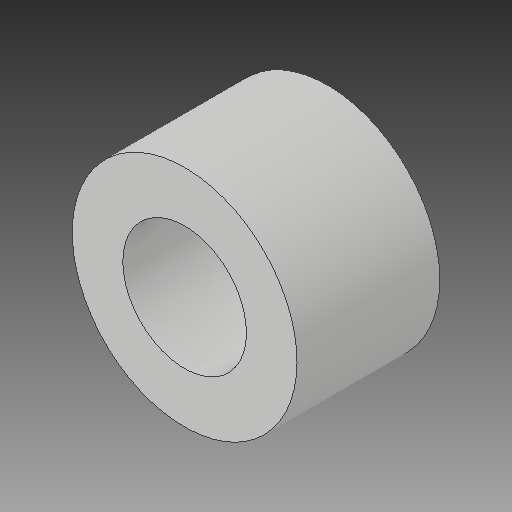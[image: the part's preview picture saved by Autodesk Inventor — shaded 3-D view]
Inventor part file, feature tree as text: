
AUTODESK INVENTOR PART (.ipt)
format: ipt  version: 2018 (Build 220112000, 112)  size: 101,888 bytes
history: native  units: mm
features: other x3, sketch x1
ambient origin geometry x8: Origin, YZ Plane, XZ Plane, XY Plane, X Axis, Y Axis, Z Axis, Center Point
bodies: Solid1 (feature_tree)
feature tree (4):
  other  "Small-Aluminium-Spacer_MIR1.ipt"
  other  "Solid1::Small-Aluminium-Spacer_MIR1.ipt"
  other  "TaggingFeature1"
  sketch  "Sketch1"  dims[d0=10.0mm]
